# Revit family: Haworth_BeHold-Design_TambourDoorCabinet_BaseElement_EU_PRELIMINARY
name_source: partatom
category: Furniture Systems
units: mm (PartAtom-declared; Revit-internal decimal feet)

## family parameters
Always vertical = Yes
Cut with Voids When Loaded = No
OmniClass Number = 23.40.70.14.64.21
OmniClass Title = Systems Furniture
Part Type = Normal
Room Calculation Point = No
Round Connector Dimension = Use Diameter
Shared = No
Work Plane-Based = No

## types (6) — shared parameters
Actual Depth = 43 cm
Assembly Code = E2020200
Custom Size = Yes
Description = Haworth - BeHold Design - Tambour Door Cabinet - Base Element
Glide Finish = Haworth _ Polymer _ Undecided
Manufacturer = Haworth
Max. Height = 153 cm
Max. Width = 160 cm
Min. Height = 50 cm
Min. Width = 80 cm
Model = ESDTDGE
Plinth Finish = Haworth _ Polymer _ Undecided
Pull Finish = Haworth _ Polymer _ Undecided
Revision Number = 1
Size = Verify Final Dim. w/ Haworth
Trim Finish = Haworth _ Polymer _ Undecided
URL = https://www.haworth.com
URL - Product = https://www.haworth.com
Warranty = http://www.haworth.com

## per-type parameters (varying)
| type | 100H | 1BH | 2BH | 3BH | 4BH | 74H | Actual Height | Actual Width | Casters | Door Height | Door Width | Glides | Height | Lock Offset Length | Lock Offset Side | Mounting Height | Plinth | Pull Height | Width |
| 140w 1BH | No | Yes | No | No | No | No | 50 cm | 140 cm | No | 42 cm | 68 cm | No | 50 cm | 21 cm | 70 cm | 3 cm | Yes | 17 cm | 140 cm |
| 90w 2BH | No | No | Yes | No | No | No | 87 cm | 90 cm | Yes | 79 cm | 43 cm | No | 87 cm | 40 cm | 45 cm | 3 cm | No | 54 cm | 90 cm |
| 160w 3BH | No | No | No | Yes | No | No | 124 cm | 160 cm | Yes | 116 cm | 78 cm | No | 124 cm | 58 cm | 80 cm | 3 cm | No | 91 cm | 160 cm |
| 120w 4BH | No | No | No | No | Yes | No | 153 cm | 120 cm | No | 145 cm | 58 cm | Yes | 153 cm | 73 cm | 60 cm | 0 cm | No | 120 cm | 120 cm |
| 80w 74h | No | No | No | No | No | Yes | 74 cm | 80 cm | No | 66 cm | 38 cm | No | 74 cm | 33 cm | 40 cm | 3 cm | Yes | 41 cm | 80 cm |
| 100w 100h | Yes | No | No | No | No | No | 100 cm | 100 cm | No | 92 cm | 48 cm | Yes | 100 cm | 46 cm | 50 cm | 0 cm | No | 67 cm | 100 cm |

## geometry (parser evidence)
native form markers: Sweep x18
no freeform markers — native parametric forms only
